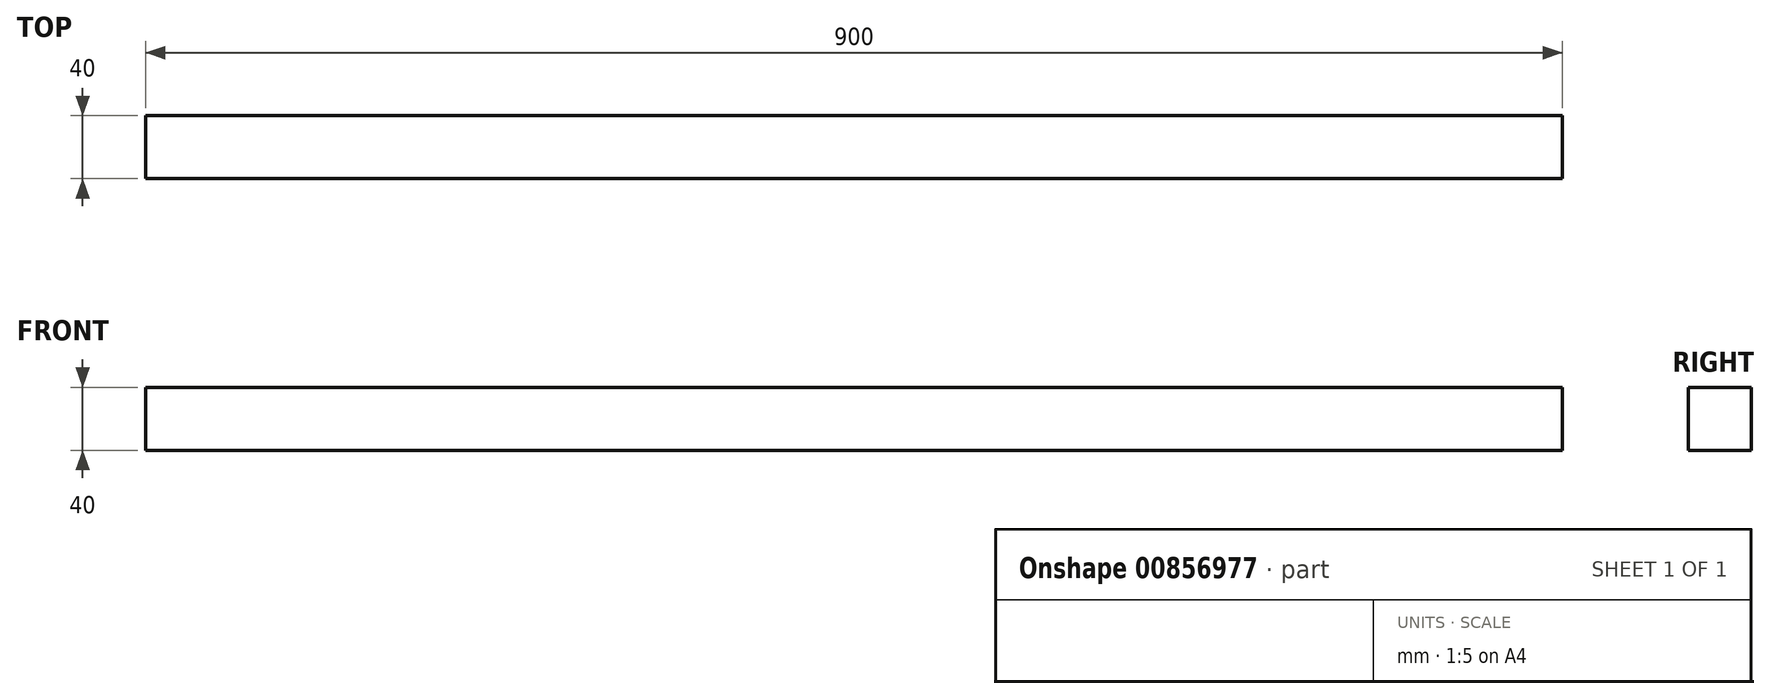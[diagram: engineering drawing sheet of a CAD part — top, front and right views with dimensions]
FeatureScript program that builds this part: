
annotation { "Feature Type Name" : "Feature", "Feature Type Description" : "" }
export const myFeature = defineFeature(function(context is Context, id is Id, definition is map)
    precondition{}
    {
        {
            var Q0;
            Q0=qCreatedBy(makeId("Right.planeOp"),FACE);
            var sketch = newSketch(context, id + "F0", { "sketchPlane" : qUnion([Q0])});
            skLineSegment(sketch, "E0.bottom", {"start": v(0, 0) * mm, "end": v(40, 0) * mm});
            skLineSegment(sketch, "E0.top", {"start": v(0, -40) * mm, "end": v(40, -40) * mm});
            skLineSegment(sketch, "E0.left", {"start": v(0, 0) * mm, "end": v(0, -40) * mm});
            skLineSegment(sketch, "E0.right", {"start": v(40, 0) * mm, "end": v(40, -40) * mm});
            skSolve(sketch);
        }
        {
            var Q0;
            Q0=makeQuery(id+"F0.imprint","IMPRINT",FACE,{"disambiguationData":[TD([[makeQuery(id+"F0.imprint","IMPRINT",EDGE,{"derivedFrom":sQuery(id+"F0.wireOp",EDGE,"E0.bottom")}),-1.0]])]});
            extrude(context, id + "F1", {"entities" : qUnion([Q0]), "depth" : 900 * mm, "offsetDistance" : 25 * mm});
        }
        {
            var Q0;
            Q0=makeQuery(id+"F1.opExtrude","SWEPT_FACE",FACE,{"disambiguationData":[OSD([sQuery(id+"F0.wireOp",EDGE,"E0.right")])]});
            var sketch = newSketch(context, id + "F2", { "sketchPlane" : qUnion([Q0])});
            skLineSegment(sketch, "E1", {"start": v(0, -20) * mm, "end": v(-20, -20) * mm, "construction": true});
            skLineSegment(sketch, "E2", {"start": v(-900, -20) * mm, "end": v(-880, -20) * mm, "construction": true});
            skSolve(sketch);
        }
        {
            var Q0;
            Q0=makeQuery(id+"F1.opExtrude","SWEPT_FACE",FACE,{"disambiguationData":[OSD([sQuery(id+"F0.wireOp",EDGE,"E0.left")])]});
            var sketch = newSketch(context, id + "F3", { "sketchPlane" : qUnion([Q0])});
            skLineSegment(sketch, "E3", {"start": v(0, -20) * mm, "end": v(20, -20) * mm, "construction": true});
            skLineSegment(sketch, "E4", {"start": v(900, -20) * mm, "end": v(880, -20) * mm, "construction": true});
            skSolve(sketch);
        }
    });
